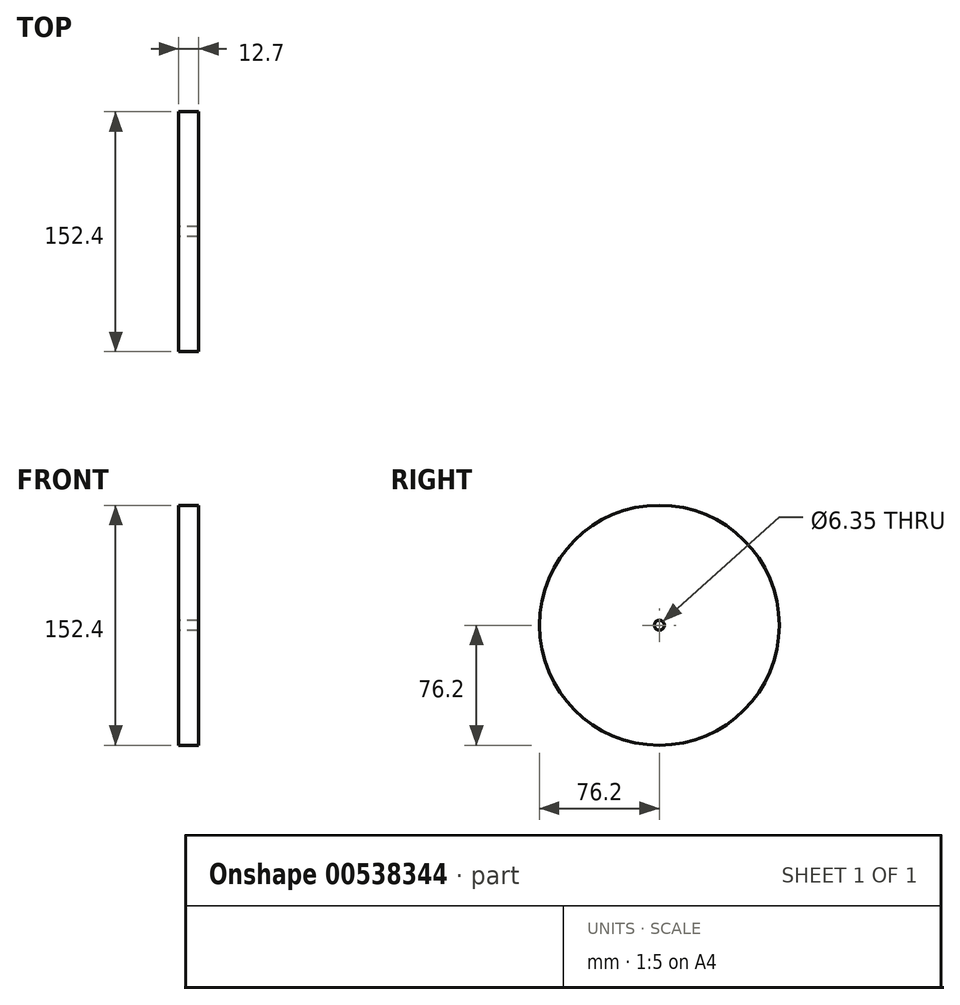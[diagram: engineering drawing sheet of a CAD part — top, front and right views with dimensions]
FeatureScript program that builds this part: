
annotation { "Feature Type Name" : "Feature", "Feature Type Description" : "" }
export const myFeature = defineFeature(function(context is Context, id is Id, definition is map)
    precondition{}
    {
        {
            var Q0;
            Q0=qCreatedBy(makeId("Right.planeOp"),FACE);
            var sketch = newSketch(context, id + "F0", { "sketchPlane" : qUnion([Q0])});
            skCircle(sketch, "E0", {"center": v(0, 0) * mm, "radius": 76.2 * mm});
            skCircle(sketch, "E1", {"center": v(0, 0) * mm, "radius": 3.18 * mm});
            skSolve(sketch);
        }
        {
            var Q0;
            Q0=makeQuery(id+"F0.imprint","IMPRINT",FACE,{"disambiguationData":[TD([[makeQuery(id+"F0.imprint","IMPRINT",EDGE,{"derivedFrom":sQuery(id+"F0.wireOp",EDGE,"E0")}),1.0]])]});
            extrude(context, id + "F1", {"entities" : qUnion([Q0]), "endBound" : BoundingType.SYMMETRIC, "depth" : 12.7 * mm, "offsetDistance" : 25.4 * mm});
        }
    });
